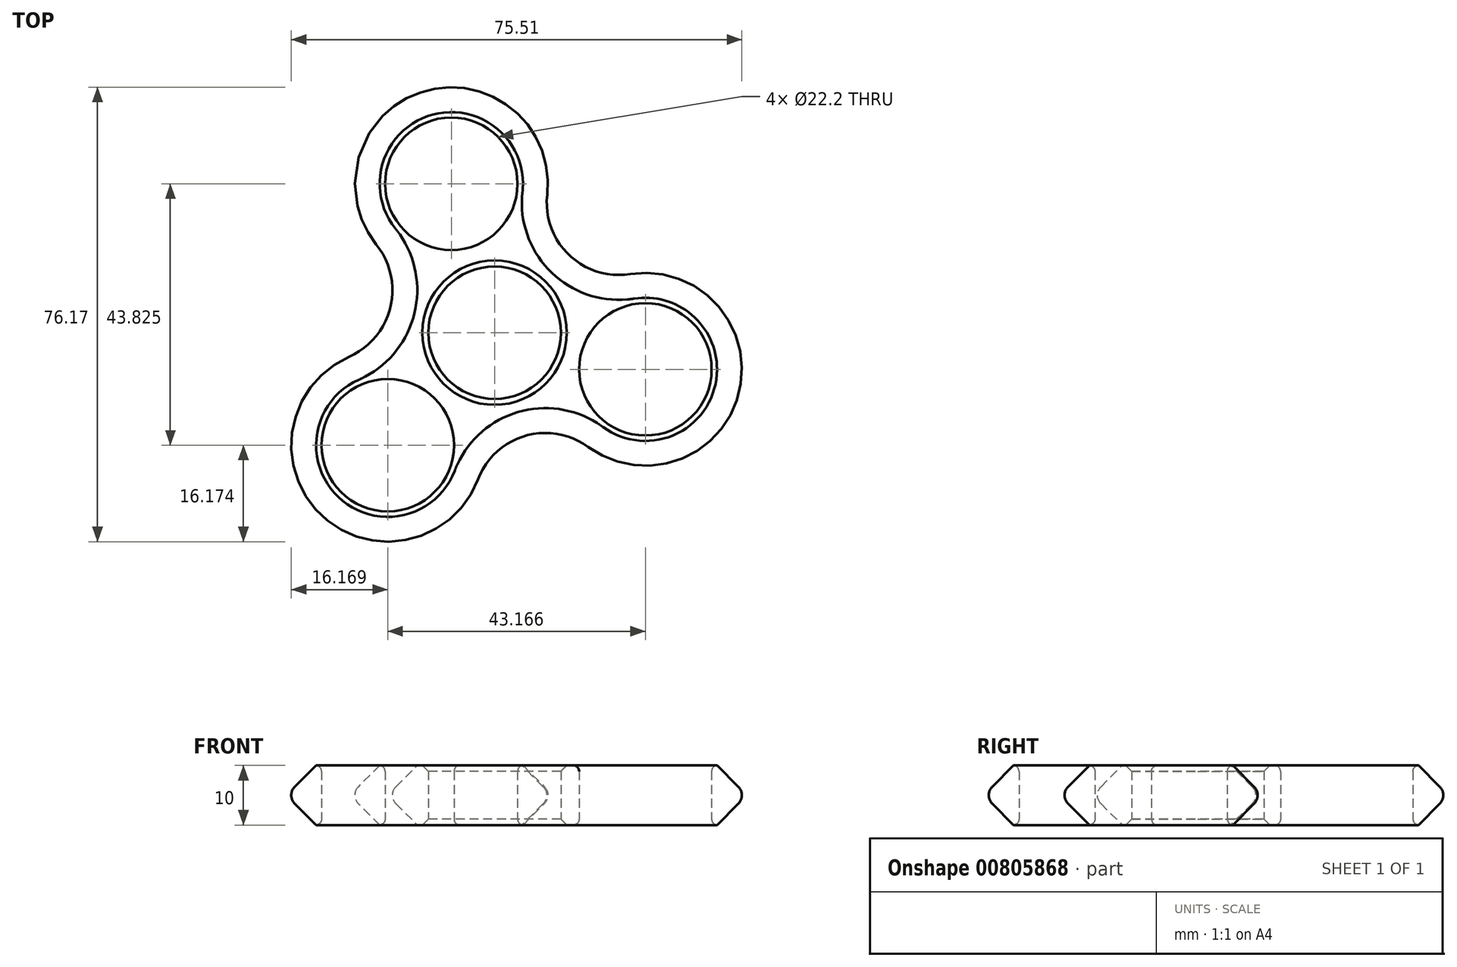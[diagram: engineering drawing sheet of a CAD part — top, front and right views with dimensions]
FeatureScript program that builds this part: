
annotation { "Feature Type Name" : "Feature", "Feature Type Description" : "" }
export const myFeature = defineFeature(function(context is Context, id is Id, definition is map)
    precondition{}
    {
        {
            var Q0;
            Q0=qCreatedBy(makeId("Top.planeOp"),FACE);
            var sketch = newSketch(context, id + "F0", { "sketchPlane" : qUnion([Q0])});
            skCircle(sketch, "E0", {"center": v(0, 0) * mm, "radius": 11.1 * mm});
            skCircle(sketch, "E1", {"center": v(-7.25, 24.97) * mm, "radius": 11.1 * mm});
            skCircle(sketch, "E2", {"center": v(25.26, -6.14) * mm, "radius": 11.1 * mm});
            skCircle(sketch, "E3", {"center": v(-17.9, -18.86) * mm, "radius": 11.1 * mm});
            skCircle(sketch, "E4", {"center": v(-17.9, -18.86) * mm, "radius": 17 * mm});
            skCircle(sketch, "E5", {"center": v(25.26, -6.14) * mm, "radius": 17 * mm});
            skCircle(sketch, "E6", {"center": v(-7.25, 24.97) * mm, "radius": 17 * mm});
            skArc(sketch, "E7", {"start": v(15.2, -19.83) * mm, "mid": v(5.33, -18.1) * mm, "end": v(-2.01, -24.9) * mm});
            skArc(sketch, "E8", {"start": v(9.64, 23.05) * mm, "mid": v(13.04, 13.64) * mm, "end": v(22.6, 10.65) * mm});
            skArc(sketch, "E9", {"start": v(-24.76, -3.3) * mm, "mid": v(-18.28, 4.44) * mm, "end": v(-20.49, 14.3) * mm});
            skCircle(sketch, "E10", {"center": v(0, 0) * mm, "radius": 12 * mm});
            skSolve(sketch);
        }
        {
            var Q0;
            Q0=makeQuery(id+"F0.imprint","IMPRINT",FACE,{"disambiguationData":[TD([[makeQuery(id+"F0.imprint","IMPRINT",EDGE,{"derivedFrom":sQuery(id+"F0.wireOp",EDGE,"E1")}),-1.0]])]});
            var Q1;
            {var subQ5=sQuery(id+"F0.wireOp",EDGE,"E8");Q1=makeQuery(id+"F0.imprint","IMPRINT",FACE,{"disambiguationData":[TD([[makeQuery(id+"F0.imprint","IMPRINT",EDGE,{"derivedFrom":subQ5}),-1.0]])]});}
            var Q2;
            Q2=makeQuery(id+"F0.imprint","IMPRINT",FACE,{"disambiguationData":[TD([[makeQuery(id+"F0.imprint","IMPRINT",EDGE,{"derivedFrom":sQuery(id+"F0.wireOp",EDGE,"E2")}),-1.0]])]});
            var Q3;
            {var subQ5=sQuery(id+"F0.wireOp",EDGE,"E7");Q3=makeQuery(id+"F0.imprint","IMPRINT",FACE,{"disambiguationData":[TD([[makeQuery(id+"F0.imprint","IMPRINT",EDGE,{"derivedFrom":subQ5}),-1.0]])]});}
            var Q4;
            Q4=makeQuery(id+"F0.imprint","IMPRINT",FACE,{"disambiguationData":[TD([[makeQuery(id+"F0.imprint","IMPRINT",EDGE,{"derivedFrom":sQuery(id+"F0.wireOp",EDGE,"E3")}),-1.0]])]});
            var Q5;
            {var subQ5=sQuery(id+"F0.wireOp",EDGE,"E9");Q5=makeQuery(id+"F0.imprint","IMPRINT",FACE,{"disambiguationData":[TD([[makeQuery(id+"F0.imprint","IMPRINT",EDGE,{"derivedFrom":subQ5}),-1.0]])]});}
            var Q6;
            {var subQ0=sQuery(id+"F0.wireOp",EDGE,"E6");var subQ1=sQuery(id+"F0.wireOp",EDGE,"E0");var subQ2=makeQuery(id+"F0.imprint","INTERSECT",VERTEX,{"disambiguationData":[OD(0.0)],"derivedFrom":[subQ1,subQ0]});Q6=makeQuery(id+"F0.imprint","IMPRINT",FACE,{"disambiguationData":[TD([[makeQuery(id+"F0.imprint","IMPRINT",EDGE,{"disambiguationData":[TD([[subQ2,-1.0]])],"derivedFrom":subQ1}),-1.0]])]});}
            var Q7;
            {var subQ0=sQuery(id+"F0.wireOp",EDGE,"E6");var subQ1=sQuery(id+"F0.wireOp",EDGE,"E0");var subQ2=makeQuery(id+"F0.imprint","INTERSECT",VERTEX,{"disambiguationData":[OD(1.0)],"derivedFrom":[subQ1,subQ0]});Q7=makeQuery(id+"F0.imprint","IMPRINT",FACE,{"disambiguationData":[TD([[makeQuery(id+"F0.imprint","IMPRINT",EDGE,{"disambiguationData":[TD([[subQ2,-1.0]])],"derivedFrom":subQ1}),-1.0]])]});}
            var Q8;
            {var subQ0=sQuery(id+"F0.wireOp",EDGE,"E6");var subQ1=sQuery(id+"F0.wireOp",EDGE,"E0");var subQ2=makeQuery(id+"F0.imprint","INTERSECT",VERTEX,{"disambiguationData":[OD(0.0)],"derivedFrom":[subQ1,subQ0]});Q8=makeQuery(id+"F0.imprint","IMPRINT",FACE,{"disambiguationData":[TD([[makeQuery(id+"F0.imprint","IMPRINT",EDGE,{"disambiguationData":[TD([[subQ2,1.0]])],"derivedFrom":subQ1}),-1.0]])]});}
            var Q9;
            {var subQ0=sQuery(id+"F0.wireOp",EDGE,"E5");var subQ1=sQuery(id+"F0.wireOp",EDGE,"E0");var subQ2=makeQuery(id+"F0.imprint","INTERSECT",VERTEX,{"disambiguationData":[OD(0.0)],"derivedFrom":[subQ1,subQ0]});Q9=makeQuery(id+"F0.imprint","IMPRINT",FACE,{"disambiguationData":[TD([[makeQuery(id+"F0.imprint","IMPRINT",EDGE,{"disambiguationData":[TD([[subQ2,1.0]])],"derivedFrom":subQ1}),-1.0]])]});}
            var Q10;
            {var subQ0=sQuery(id+"F0.wireOp",EDGE,"E4");var subQ1=sQuery(id+"F0.wireOp",EDGE,"E0");var subQ2=makeQuery(id+"F0.imprint","INTERSECT",VERTEX,{"disambiguationData":[OD(1.0)],"derivedFrom":[subQ1,subQ0]});Q10=makeQuery(id+"F0.imprint","IMPRINT",FACE,{"disambiguationData":[TD([[makeQuery(id+"F0.imprint","IMPRINT",EDGE,{"disambiguationData":[TD([[subQ2,-1.0]])],"derivedFrom":subQ1}),-1.0]])]});}
            var Q11;
            {var subQ0=sQuery(id+"F0.wireOp",EDGE,"E4");var subQ1=sQuery(id+"F0.wireOp",EDGE,"E0");var subQ2=makeQuery(id+"F0.imprint","INTERSECT",VERTEX,{"disambiguationData":[OD(0.0)],"derivedFrom":[subQ1,subQ0]});Q11=makeQuery(id+"F0.imprint","IMPRINT",FACE,{"disambiguationData":[TD([[makeQuery(id+"F0.imprint","IMPRINT",EDGE,{"disambiguationData":[TD([[subQ2,-1.0]])],"derivedFrom":subQ1}),-1.0]])]});}
            extrude(context, id + "F1", {"entities" : qUnion([Q0, Q1, Q2, Q3, Q4, Q5, Q6, Q7, Q8, Q9, Q10, Q11]), "depth" : 10 * mm, "offsetDistance" : 25 * mm});
        }
        {
            var Q0;
            Q0=makeQuery(id+"F1.opExtrude","CAP_EDGE",EDGE,{"disambiguationData":[OSD([sQuery(id+"F0.wireOp",EDGE,"E4")])],"isStart":false});
            var Q1;
            Q1=makeQuery(id+"F1.opExtrude","CAP_EDGE",EDGE,{"disambiguationData":[OSD([sQuery(id+"F0.wireOp",EDGE,"E5")])],"isStart":true});
            chamfer(context, id + "F2", {"entities" : qUnion([Q0, Q1]), "width" : 5 * mm, "tangentPropagation" : true});
        }
        {
            var Q0;
            Q0=makeQuery(id+"F1.opExtrude","CAP_EDGE",EDGE,{"disambiguationData":[OSD([sQuery(id+"F0.wireOp",EDGE,"E2")])],"isStart":false});
            var Q1;
            Q1=makeQuery(id+"F1.opExtrude","CAP_EDGE",EDGE,{"disambiguationData":[OSD([sQuery(id+"F0.wireOp",EDGE,"E1")])],"isStart":false});
            var Q2;
            Q2=makeQuery(id+"F1.opExtrude","CAP_EDGE",EDGE,{"disambiguationData":[OSD([sQuery(id+"F0.wireOp",EDGE,"E3")])],"isStart":false});
            var Q3;
            Q3=makeQuery(id+"F1.opExtrude","CAP_EDGE",EDGE,{"disambiguationData":[OSD([sQuery(id+"F0.wireOp",EDGE,"E2")])],"isStart":true});
            var Q4;
            Q4=makeQuery(id+"F1.opExtrude","CAP_EDGE",EDGE,{"disambiguationData":[OSD([sQuery(id+"F0.wireOp",EDGE,"E1")])],"isStart":true});
            var Q5;
            Q5=makeQuery(id+"F1.opExtrude","CAP_EDGE",EDGE,{"disambiguationData":[OSD([sQuery(id+"F0.wireOp",EDGE,"E3")])],"isStart":true});
            fillet(context, id + "F3", {"entities" : qUnion([Q0, Q1, Q2, Q3, Q4, Q5]), "radius" : 1 * mm, "tangentPropagation" : true, "allowEdgeOverflow" : false});
        }
        {
            var Q0;
            Q0=makeQuery(id+"F1.opExtrude","CAP_EDGE",EDGE,{"disambiguationData":[OSD([sQuery(id+"F0.wireOp",EDGE,"E0")])],"isStart":true});
            var Q1;
            Q1=makeQuery(id+"F1.opExtrude","SWEPT_FACE",FACE,{"disambiguationData":[OSD([sQuery(id+"F0.wireOp",EDGE,"E0")])]});
            chamfer(context, id + "F4", {"entities" : qUnion([Q0, Q1]), "width" : 1 * mm, "tangentPropagation" : true});
        }
        {
            var Q0;
            {var subQ0=sQuery(id+"F0.wireOp",EDGE,"E7");Q0=makeQuery(id+"F2.opChamfer","BLEND_EDGE",EDGE,{"blendedFrom":[makeQuery(id+"F1.opExtrude","CAP_EDGE",EDGE,{"disambiguationData":[OSD([subQ0])],"isStart":true}),makeQuery(id+"F1.opExtrude","CAP_EDGE",EDGE,{"disambiguationData":[OSD([subQ0])],"isStart":false})],"blendedInto":[]});}
            var Q1;
            {var subQ0=sQuery(id+"F0.wireOp",EDGE,"E4");Q1=makeQuery(id+"F2.opChamfer","BLEND_EDGE",EDGE,{"blendedFrom":[makeQuery(id+"F1.opExtrude","CAP_EDGE",EDGE,{"disambiguationData":[OSD([subQ0])],"isStart":true}),makeQuery(id+"F1.opExtrude","CAP_EDGE",EDGE,{"disambiguationData":[OSD([subQ0])],"isStart":false})],"blendedInto":[]});}
            var Q2;
            {var subQ0=sQuery(id+"F0.wireOp",EDGE,"E5");Q2=makeQuery(id+"F2.opChamfer","BLEND_EDGE",EDGE,{"blendedFrom":[makeQuery(id+"F1.opExtrude","CAP_EDGE",EDGE,{"disambiguationData":[OSD([subQ0])],"isStart":true}),makeQuery(id+"F1.opExtrude","CAP_EDGE",EDGE,{"disambiguationData":[OSD([subQ0])],"isStart":false})],"blendedInto":[]});}
            var Q3;
            {var subQ0=sQuery(id+"F0.wireOp",EDGE,"E6");Q3=makeQuery(id+"F2.opChamfer","BLEND_EDGE",EDGE,{"blendedFrom":[makeQuery(id+"F1.opExtrude","CAP_EDGE",EDGE,{"disambiguationData":[OSD([subQ0])],"isStart":true}),makeQuery(id+"F1.opExtrude","CAP_EDGE",EDGE,{"disambiguationData":[OSD([subQ0])],"isStart":false})],"blendedInto":[]});}
            var Q4;
            {var subQ0=sQuery(id+"F0.wireOp",EDGE,"E8");Q4=makeQuery(id+"F2.opChamfer","BLEND_EDGE",EDGE,{"blendedFrom":[makeQuery(id+"F1.opExtrude","CAP_EDGE",EDGE,{"disambiguationData":[OSD([subQ0])],"isStart":true}),makeQuery(id+"F1.opExtrude","CAP_EDGE",EDGE,{"disambiguationData":[OSD([subQ0])],"isStart":false})],"blendedInto":[]});}
            var Q5;
            {var subQ0=sQuery(id+"F0.wireOp",EDGE,"E9");Q5=makeQuery(id+"F2.opChamfer","BLEND_EDGE",EDGE,{"blendedFrom":[makeQuery(id+"F1.opExtrude","CAP_EDGE",EDGE,{"disambiguationData":[OSD([subQ0])],"isStart":true}),makeQuery(id+"F1.opExtrude","CAP_EDGE",EDGE,{"disambiguationData":[OSD([subQ0])],"isStart":false})],"blendedInto":[]});}
            fillet(context, id + "F5", {"entities" : qUnion([Q0, Q1, Q2, Q3, Q4, Q5]), "radius" : 2 * mm, "tangentPropagation" : true, "allowEdgeOverflow" : false});
        }
    });
